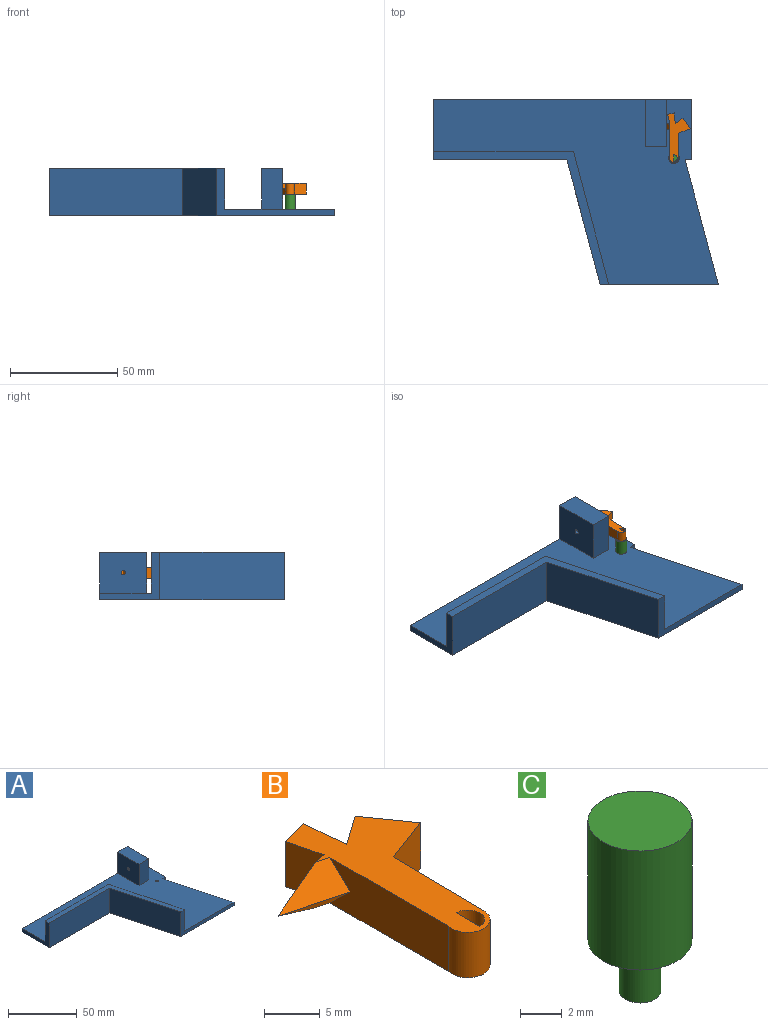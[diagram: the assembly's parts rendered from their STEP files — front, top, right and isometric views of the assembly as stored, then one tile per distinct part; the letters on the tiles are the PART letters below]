
ASSEMBLY  parts=3 mates=2
PART A: 21 faces, bbox 132.5x86x22 mm
  f0: cylinder r=1mm len=7mm, axis (1,0,0), area 44mm2, adj f15,f19
  f1: plane 132.52x85.96mm, normal (0,0,1), area 5830.9mm2, adj f4,f5,f6,f7,f8,f9,f11,f12
  f2: plane 61.99x22mm, normal (0,-1,0), area 1363.9mm2, adj f3,f9,f10,f13
  f3: plane 57.96x22mm, normal (-0.97,-0.26,0), area 1320mm2, adj f2,f4,f10,f13
  f4: plane 55x22mm, normal (0,-1,0), area 241mm2, adj f1,f3,f5,f10,f11,f13
  f5: plane 57.96x15.53mm, normal (0.97,0.26,0), area 180mm2, adj f1,f4,f6,f10
  f6: plane 3.01x3mm, normal (0,-1,0), area 9mm2, adj f1,f5,f7,f10
  f7: plane 28x3mm, normal (1,0,0), area 84mm2, adj f1,f6,f8,f10
  f8: plane 120x22mm, normal (0,1,0), area 550mm2, adj f1,f7,f9,f10,f14,f15,f17
  f9: plane 28x22mm, normal (-1,0,0), area 160mm2, adj f1,f2,f8,f10,f12,f13
  f10: plane 132.52x85.96mm, normal (0,0,-1), area 6544.4mm2, adj f2,f3,f4,f5,f6,f7,f8,f9
  f11: plane 61.82x19mm, normal (0.97,0.26,0), area 1215.3mm2, adj f1,f4,f12,f13
  f12: plane 65.1x19mm, normal (0,1,0), area 1236.9mm2, adj f1,f9,f11,f13
  f13: plane 81.52x61.96mm, normal (0,0,1), area 493.5mm2, adj f2,f3,f4,f9,f11,f12
  f14: plane 22x19mm, normal (1,0,0), area 398.4mm2, adj f1,f8,f16,f17,f18
  f15: plane 22x19mm, normal (-1,0,0), area 414.9mm2, adj f0,f1,f8,f16,f17
  f16: plane 19x10mm, normal (0,-1,0), area 190mm2, adj f1,f14,f15,f17
  f17: plane 22x10mm, normal (0,0,1), area 220mm2, adj f8,f14,f15,f16
  f18: cylinder r=2.5mm len=5mm, axis (1,0,0), area 47.1mm2, adj f14,f19
  f19: plane 5x5mm, normal (1,0,0), area 16.5mm2, adj f0,f18
  f20: cylinder r=1mm len=3mm, axis (0,0,1), area 18.8mm2, adj f1,f10
PART B: 16 faces, bbox 16.9x23x5 mm
  f0: cylinder r=2mm len=5mm, axis (0,0,-1), area 33.8mm2, adj f1,f11,f12,f13
  f1: plane 11.67x5mm, normal (1,-0.02,0), area 58.4mm2, adj f0,f2,f12,f13
  f2: plane 5.49x5mm, normal (0.35,-0.94,0), area 29.3mm2, adj f1,f3,f12,f13
  f3: plane 5x4.89mm, normal (0.82,0.58,0), area 29.9mm2, adj f2,f4,f12,f13
  f4: plane 5x3.64mm, normal (-0.58,0.82,0), area 22.3mm2, adj f3,f5,f12,f13
  f5: plane 5.02x5mm, normal (1,0.09,0), area 25.2mm2, adj f4,f6,f12,f13
  f6: plane 5x3.13mm, normal (-0.24,0.97,0), area 16.1mm2, adj f5,f7,f12,f13
  f7: plane 5x3.97mm, normal (-0.97,-0.24,0), area 20.5mm2, adj f6,f8,f12,f13
  f8: plane 7.2x5mm, normal (-0.18,0.98,0), area 21.8mm2, adj f7,f12,f13,f14,f15
  f9: plane 5x3mm, normal (1,0,0), area 15mm2, adj f10,f12,f13
  f10: cylinder r=1.5mm len=5mm, axis (0,0,-1), area 23.6mm2, adj f9,f12,f13
  f11: plane 15.16x5mm, normal (-1,0,0), area 69.3mm2, adj f0,f12,f13,f14,f15
  f12: plane 23.04x11.06mm, normal (0,0,1), area 105mm2, adj f0,f1,f2,f3,f4,f5,f6,f7
  f13: plane 23.04x11.06mm, normal (0,0,-1), area 105mm2, adj f0,f1,f2,f3,f4,f5,f6,f7
  f14: plane 7.27x2.97mm, normal (-0.18,-0.68,0.71), area 15.9mm2, adj f8,f11,f12,f15
  f15: plane 7.27x2.97mm, normal (-0.18,-0.68,-0.71), area 15.9mm2, adj f8,f11,f13,f14
PART C: 5 faces, bbox 5x5x10 mm
  f0: cylinder r=1mm len=3mm, axis (0,0,-1), area 18.8mm2, adj f1,f4
  f1: plane 2x2mm, normal (0,0,-1), area 3.1mm2, adj f0
  f2: cylinder r=2.5mm len=7mm, axis (0,0,-1), area 110mm2, adj f3,f4
  f3: plane 5x5mm, normal (0,0,1), area 19.6mm2, adj f2
  f4: plane 5x5mm, normal (0,0,-1), area 16.5mm2, adj f0,f2
PLACE A t=(16.32,1.17,-3)mm
PLACE B t=(-3.1,-8.81,7)mm
PLACE C t=(0.6,6.09,-3)mm
MATE revolute C.f0 <-> A.f20  axis (0,0,-1) through (68.17,-12.03,0)mm
MATE fastened B.f0 <-> C.f0  axis (0,0,-1) through (68.17,-12.03,7)mm
